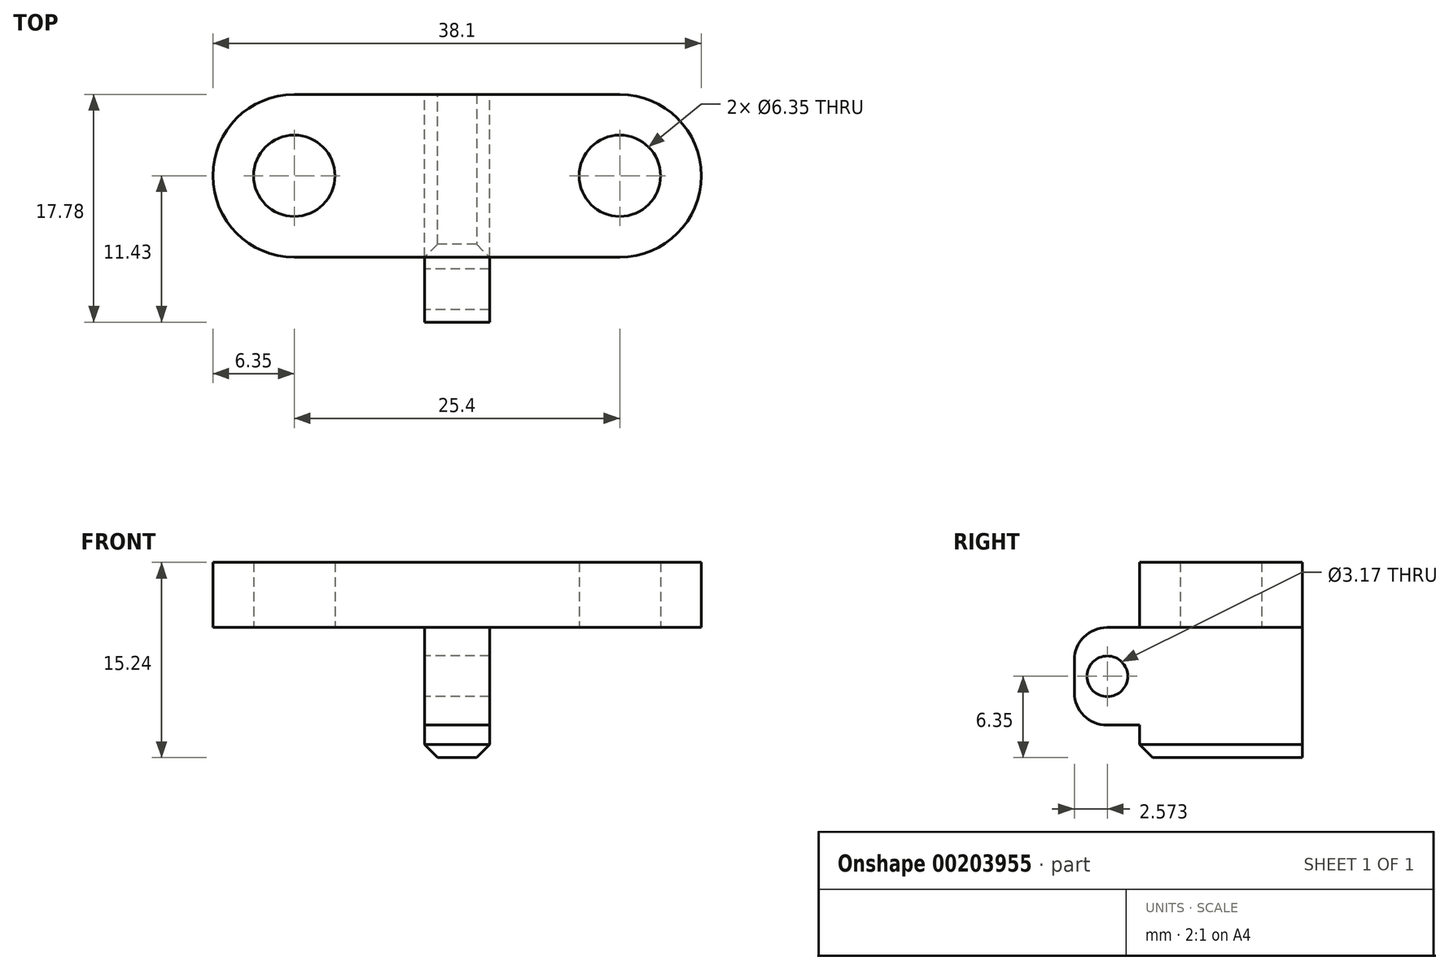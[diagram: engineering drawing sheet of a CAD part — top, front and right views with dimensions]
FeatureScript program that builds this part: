
annotation { "Feature Type Name" : "Feature", "Feature Type Description" : "" }
export const myFeature = defineFeature(function(context is Context, id is Id, definition is map)
    precondition{}
    {
        {
            var Q0;
            Q0=qCreatedBy(makeId("Top.planeOp"),FACE);
            var sketch = newSketch(context, id + "F0", { "sketchPlane" : qUnion([Q0])});
            skLineSegment(sketch, "E0", {"start": v(0, 0) * mm, "end": v(-25.4, 0) * mm});
            skArc(sketch, "E1", {"start": v(-25.4, 6.35) * mm, "mid": v(-31.75, 0) * mm, "end": v(-25.4, -6.35) * mm});
            skCircle(sketch, "E2", {"center": v(-25.4, 0) * mm, "radius": 3.18 * mm});
            skArc(sketch, "E3", {"start": v(0, -6.35) * mm, "mid": v(6.35, 0) * mm, "end": v(0, 6.35) * mm});
            skCircle(sketch, "E4", {"center": v(0, 0) * mm, "radius": 3.18 * mm});
            skLineSegment(sketch, "E5", {"start": v(-25.4, 6.35) * mm, "end": v(0, 6.35) * mm});
            skLineSegment(sketch, "E6", {"start": v(-25.4, -6.35) * mm, "end": v(0, -6.35) * mm});
            skSolve(sketch);
        }
        {
            var Q0;
            Q0=makeQuery(id+"F0.imprint","IMPRINT",FACE,{"disambiguationData":[TD([[makeQuery(id+"F0.imprint","IMPRINT",EDGE,{"derivedFrom":sQuery(id+"F0.wireOp",EDGE,"E1")}),1.0]])]});
            extrude(context, id + "F1", {"entities" : qUnion([Q0]), "depth" : 22.86 * mm});
        }
        {
            var Q0;
            Q0=makeQuery(id+"F1.opExtrude","SWEPT_FACE",FACE,{"disambiguationData":[OSD([sQuery(id+"F0.wireOp",EDGE,"E5")])]});
            var sketch = newSketch(context, id + "F2", { "sketchPlane" : qUnion([Q0])});
            skLineSegment(sketch, "E7", {"start": v(12.7, 22.86) * mm, "end": v(12.7, 11.43) * mm});
            skPoint(sketch, "E7.endSnap0", {"position": v(12.7, 0) * mm});
            skLineSegment(sketch, "E8", {"start": v(12.7, 11.43) * mm, "end": v(-6.35, 11.43) * mm});
            skLineSegment(sketch, "E9", {"start": v(-6.35, 11.43) * mm, "end": v(6.35, 11.43) * mm});
            skLineSegment(sketch, "E10.top", {"start": v(-6.35, 5.08) * mm, "end": v(6.35, 5.08) * mm});
            skLineSegment(sketch, "E10.left", {"start": v(-6.35, 11.43) * mm, "end": v(-6.35, 5.08) * mm});
            skLineSegment(sketch, "E10.right", {"start": v(6.35, 11.43) * mm, "end": v(6.35, 5.08) * mm});
            skLineSegment(sketch, "E11.top", {"start": v(-6.35, 17.78) * mm, "end": v(6.35, 17.78) * mm});
            skLineSegment(sketch, "E11.left", {"start": v(-6.35, 11.43) * mm, "end": v(-6.35, 17.78) * mm});
            skLineSegment(sketch, "E11.right", {"start": v(6.35, 11.43) * mm, "end": v(6.35, 17.78) * mm});
            skLineSegment(sketch, "E12", {"start": v(12.7, 11.43) * mm, "end": v(19.05, 11.43) * mm});
            skLineSegment(sketch, "E13.bottom", {"start": v(19.05, 11.43) * mm, "end": v(32.2, 11.43) * mm});
            skLineSegment(sketch, "E13.top", {"start": v(19.05, 17.78) * mm, "end": v(32.2, 17.78) * mm});
            skLineSegment(sketch, "E13.left", {"start": v(19.05, 11.43) * mm, "end": v(19.05, 17.78) * mm});
            skLineSegment(sketch, "E13.right", {"start": v(32.2, 11.43) * mm, "end": v(32.2, 17.78) * mm});
            skLineSegment(sketch, "E14.top", {"start": v(19.05, 5.08) * mm, "end": v(32.2, 5.08) * mm});
            skLineSegment(sketch, "E14.left", {"start": v(19.05, 11.43) * mm, "end": v(19.05, 5.08) * mm});
            skLineSegment(sketch, "E14.right", {"start": v(32.2, 11.43) * mm, "end": v(32.2, 5.08) * mm});
            skSolve(sketch);
        }
        {
            var Q0;
            {var subQ0=sQuery(id+"F2.wireOp",EDGE,"E10.left");Q0=makeQuery(id+"F2.imprint","IMPRINT",FACE,{"disambiguationData":[TD([[makeQuery(id+"F2.imprint","IMPRINT",EDGE,{"derivedFrom":subQ0}),1.0]])]});}
            var Q1;
            {var subQ0=sQuery(id+"F2.wireOp",EDGE,"E13.right");Q1=makeQuery(id+"F2.imprint","IMPRINT",FACE,{"disambiguationData":[TD([[makeQuery(id+"F2.imprint","IMPRINT",EDGE,{"derivedFrom":subQ0}),1.0]])]});}
            var Q2;
            {var subQ0=sQuery(id+"F2.wireOp",EDGE,"E14.right");Q2=makeQuery(id+"F2.imprint","IMPRINT",FACE,{"disambiguationData":[TD([[makeQuery(id+"F2.imprint","IMPRINT",EDGE,{"derivedFrom":subQ0}),-1.0]])]});}
            var Q3;
            {var subQ0=sQuery(id+"F2.wireOp",EDGE,"E10.right");Q3=makeQuery(id+"F2.imprint","IMPRINT",FACE,{"disambiguationData":[TD([[makeQuery(id+"F2.imprint","IMPRINT",EDGE,{"derivedFrom":subQ0}),-1.0]])]});}
            var Q4;
            {var subQ0=sQuery(id+"F2.wireOp",EDGE,"E11.right");Q4=makeQuery(id+"F2.imprint","IMPRINT",FACE,{"disambiguationData":[TD([[makeQuery(id+"F2.imprint","IMPRINT",EDGE,{"derivedFrom":subQ0}),1.0]])]});}
            var Q5;
            {var subQ0=sQuery(id+"F2.wireOp",EDGE,"E13.left");Q5=makeQuery(id+"F2.imprint","IMPRINT",FACE,{"disambiguationData":[TD([[makeQuery(id+"F2.imprint","IMPRINT",EDGE,{"derivedFrom":subQ0}),-1.0]])]});}
            var Q6;
            {var subQ0=sQuery(id+"F2.wireOp",EDGE,"E14.left");Q6=makeQuery(id+"F2.imprint","IMPRINT",FACE,{"disambiguationData":[TD([[makeQuery(id+"F2.imprint","IMPRINT",EDGE,{"derivedFrom":subQ0}),1.0]])]});}
            var Q7;
            {var subQ0=sQuery(id+"F2.wireOp",EDGE,"E11.left");Q7=makeQuery(id+"F2.imprint","IMPRINT",FACE,{"disambiguationData":[TD([[makeQuery(id+"F2.imprint","IMPRINT",EDGE,{"derivedFrom":subQ0}),-1.0]])]});}
            extrude(context, id + "F3", {"entities" : qUnion([Q0, Q1, Q2, Q3, Q4, Q5, Q6, Q7]), "operationType" : NewBodyOperationType.REMOVE, "oppositeDirection" : true, "depth" : 25.4 * mm});
        }
        {
            var Q0;
            Q0=makeQuery(id+"F1.opExtrude","SWEPT_FACE",FACE,{"disambiguationData":[OSD([sQuery(id+"F0.wireOp",EDGE,"E5")])]});
            var sketch = newSketch(context, id + "F4", { "sketchPlane" : qUnion([Q0])});
            skLineSegment(sketch, "E15", {"start": v(12.7, 22.86) * mm, "end": v(12.7, 11.43) * mm});
            skLineSegment(sketch, "E16", {"start": v(6.35, 17.78) * mm, "end": v(-14.34, 11.9) * mm});
            skLineSegment(sketch, "E17", {"start": v(-14.34, 11.9) * mm, "end": v(-15.97, -5.65) * mm});
            skLineSegment(sketch, "E18", {"start": v(-15.97, -5.65) * mm, "end": v(34.48, -5.65) * mm});
            skLineSegment(sketch, "E19", {"start": v(34.48, -5.65) * mm, "end": v(40.58, 3.4) * mm});
            skLineSegment(sketch, "E20", {"start": v(40.58, 3.4) * mm, "end": v(19.05, 17.78) * mm});
            skLineSegment(sketch, "E21.top", {"start": v(10.16, 7.62) * mm, "end": v(15.24, 7.62) * mm});
            skLineSegment(sketch, "E21.left", {"start": v(10.16, 17.78) * mm, "end": v(10.16, 7.62) * mm});
            skLineSegment(sketch, "E21.right", {"start": v(15.24, 17.78) * mm, "end": v(15.24, 7.62) * mm});
            skLineSegment(sketch, "E22", {"start": v(6.35, 17.78) * mm, "end": v(10.16, 17.78) * mm});
            skLineSegment(sketch, "E23", {"start": v(15.24, 17.78) * mm, "end": v(19.05, 17.78) * mm});
            skSolve(sketch);
        }
        {
            var Q0;
            Q0 = qSketchRegion(id + "F4", true);
            extrude(context, id + "F5", {"entities" : qUnion([Q0]), "operationType" : NewBodyOperationType.REMOVE, "oppositeDirection" : true, "depth" : 25.4 * mm});
        }
        {
            var Q0;
            Q0=makeQuery(id+"F5.boolean.opBoolean","COPY",EDGE,{"derivedFrom":makeQuery(id+"F5.opExtrude","SWEPT_EDGE",EDGE,{"disambiguationData":[OSD([sQuery(id+"F4.wireOp",EDGE,"E21.top"),sQuery(id+"F4.wireOp",EDGE,"E21.right")])]})});
            var Q1;
            Q1=makeQuery(id+"F5.boolean.opBoolean","COPY",EDGE,{"derivedFrom":makeQuery(id+"F5.opExtrude","SWEPT_EDGE",EDGE,{"disambiguationData":[OSD([sQuery(id+"F4.wireOp",EDGE,"E21.top"),sQuery(id+"F4.wireOp",EDGE,"E21.left")])]})});
            var Q2;
            Q2=makeQuery(id+"F5.boolean.opBoolean","INTERSECT",EDGE,{"derivedFrom":[makeQuery(id+"F1.opExtrude","SWEPT_FACE",FACE,{"disambiguationData":[OSD([sQuery(id+"F0.wireOp",EDGE,"E6")])]}),makeQuery(id+"F5.opExtrude","SWEPT_FACE",FACE,{"disambiguationData":[OSD([sQuery(id+"F4.wireOp",EDGE,"E21.top")])]})]});
            var Q3;
            Q3=makeQuery(id+"F5.boolean.opBoolean","COPY",EDGE,{"derivedFrom":makeQuery(id+"F5.opExtrude","CAP_EDGE",EDGE,{"disambiguationData":[OSD([sQuery(id+"F4.wireOp",EDGE,"E21.top")])],"isStart":true})});
            chamfer(context, id + "F6", {"entities" : qUnion([Q0, Q1, Q2, Q3]), "width" : 1.02 * mm, "tangentPropagation" : true});
        }
        {
            var Q0;
            Q0=makeQuery(id+"F1.opExtrude","SWEPT_FACE",FACE,{"disambiguationData":[OSD([sQuery(id+"F0.wireOp",EDGE,"E6")])]});
            var sketch = newSketch(context, id + "F7", { "sketchPlane" : qUnion([Q0])});
            skLineSegment(sketch, "E24.bottom", {"start": v(-15.24, 17.78) * mm, "end": v(-10.16, 17.78) * mm});
            skLineSegment(sketch, "E24.top", {"start": v(-15.24, 10.16) * mm, "end": v(-10.16, 10.16) * mm});
            skLineSegment(sketch, "E24.left", {"start": v(-15.24, 17.78) * mm, "end": v(-15.24, 10.16) * mm});
            skLineSegment(sketch, "E24.right", {"start": v(-10.16, 17.78) * mm, "end": v(-10.16, 10.16) * mm});
            skSolve(sketch);
        }
        {
            var Q0;
            Q0=makeQuery(id+"F7.imprint","IMPRINT",FACE,{"disambiguationData":[TD([[makeQuery(id+"F7.imprint","IMPRINT",EDGE,{"derivedFrom":sQuery(id+"F7.wireOp",EDGE,"E24.bottom")}),-1.0]])]});
            extrude(context, id + "F8", {"entities" : qUnion([Q0]), "operationType" : NewBodyOperationType.ADD, "depth" : 5.08 * mm});
        }
        {
            var Q0;
            Q0=makeQuery(id+"F8.boolean.opBoolean","MERGE",FACE,{"derivedFrom":[makeQuery(id+"F5.boolean.opBoolean","COPY",FACE,{"derivedFrom":makeQuery(id+"F5.opExtrude","SWEPT_FACE",FACE,{"disambiguationData":[OSD([sQuery(id+"F4.wireOp",EDGE,"E21.right")])]})}),makeQuery(id+"F8.opExtrude","SWEPT_FACE",FACE,{"disambiguationData":[OSD([sQuery(id+"F7.wireOp",EDGE,"E24.left")])]})]});
            var sketch = newSketch(context, id + "F9", { "sketchPlane" : qUnion([Q0])});
            skCircle(sketch, "E25", {"center": v(8.86, 13.97) * mm, "radius": 1.59 * mm});
            skPoint(sketch, "E25.centerSnap0", {"position": v(11.43, 13.97) * mm});
            skSolve(sketch);
        }
        {
            var Q0;
            Q0=makeQuery(id+"F9.imprint","IMPRINT",FACE,{"disambiguationData":[TD([[makeQuery(id+"F9.imprint","IMPRINT",EDGE,{"derivedFrom":sQuery(id+"F9.wireOp",EDGE,"E25")}),1.0]])]});
            extrude(context, id + "F10", {"entities" : qUnion([Q0]), "operationType" : NewBodyOperationType.REMOVE, "oppositeDirection" : true, "depth" : 25.4 * mm});
        }
        {
            var Q0;
            Q0=makeQuery(id+"F8.opExtrude","CAP_EDGE",EDGE,{"disambiguationData":[OSD([sQuery(id+"F7.wireOp",EDGE,"E24.bottom")])],"isStart":false});
            var Q1;
            Q1=makeQuery(id+"F8.opExtrude","CAP_EDGE",EDGE,{"disambiguationData":[OSD([sQuery(id+"F7.wireOp",EDGE,"E24.top")])],"isStart":false});
            var Q2;
            Q2=makeQuery(id+"F8.opExtrude","CAP_EDGE",EDGE,{"disambiguationData":[OSD([sQuery(id+"F7.wireOp",EDGE,"E24.top")])],"isStart":true});
            fillet(context, id + "F11", {"entities" : qUnion([Q0, Q1, Q2]), "radius" : 2.54 * mm, "tangentPropagation" : true, "allowEdgeOverflow" : false});
        }
    });
